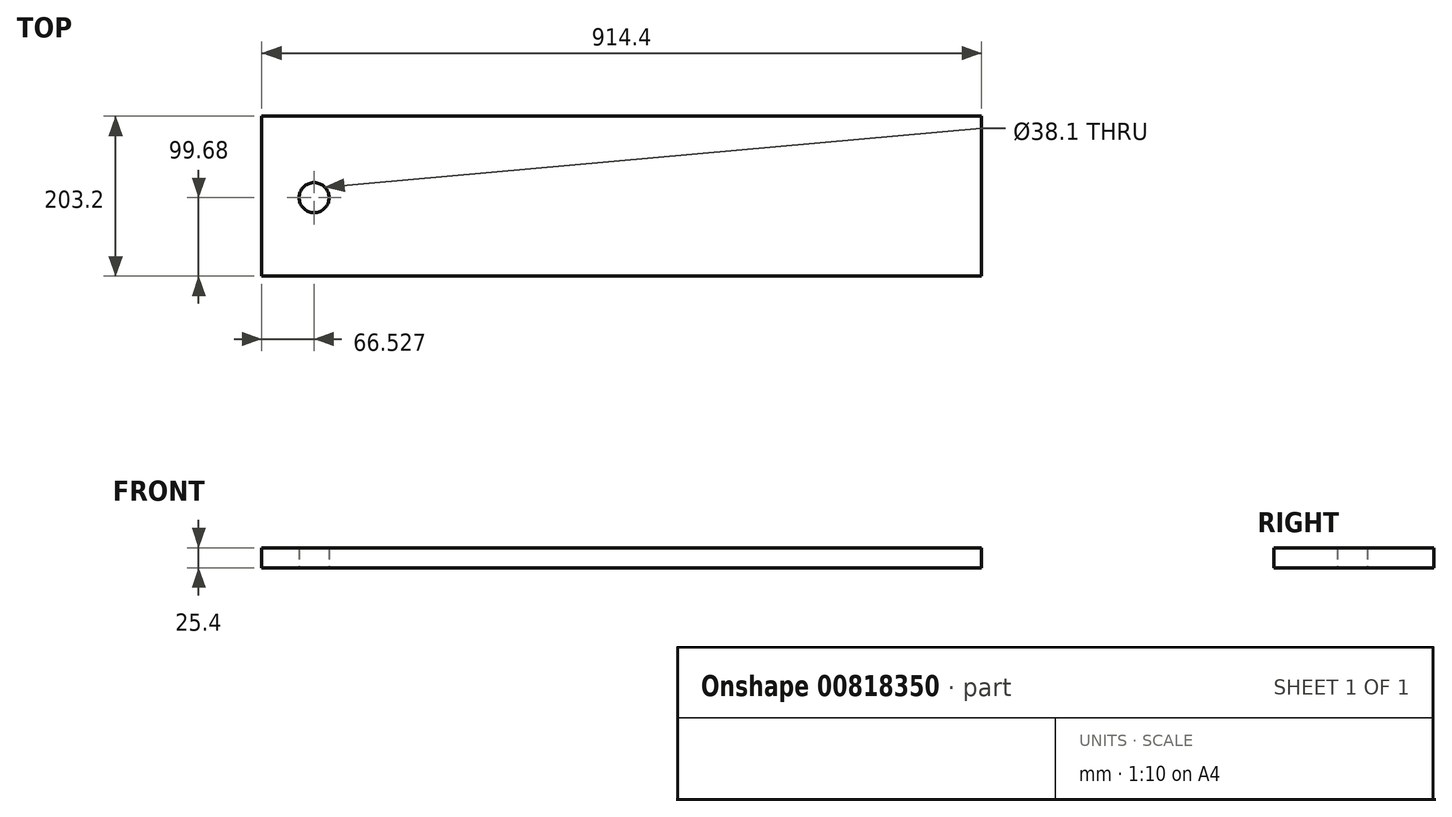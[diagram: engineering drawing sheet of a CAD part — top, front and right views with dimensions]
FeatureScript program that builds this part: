
annotation { "Feature Type Name" : "Feature", "Feature Type Description" : "" }
export const myFeature = defineFeature(function(context is Context, id is Id, definition is map)
    precondition{}
    {
        {
            var Q0;
            Q0=qCreatedBy(makeId("Top.planeOp"),FACE);
            var sketch = newSketch(context, id + "F0", { "sketchPlane" : qUnion([Q0])});
            skLineSegment(sketch, "E0.bottom", {"start": v(-470.18, 103.52) * mm, "end": v(444.22, 103.52) * mm});
            skLineSegment(sketch, "E0.top", {"start": v(-470.18, -99.68) * mm, "end": v(444.22, -99.68) * mm});
            skLineSegment(sketch, "E0.left", {"start": v(-470.18, 103.52) * mm, "end": v(-470.18, -99.68) * mm});
            skLineSegment(sketch, "E0.right", {"start": v(444.22, 103.52) * mm, "end": v(444.22, -99.68) * mm});
            skCircle(sketch, "E1", {"center": v(-403.65, 0) * mm, "radius": 19.05 * mm});
            skSolve(sketch);
        }
        {
            var Q0;
            Q0 = qSketchRegion(id + "F0", true);
            var Q1;
            Q1=makeQuery(id+"F0.imprint","IMPRINT",FACE,{"disambiguationData":[TD([[makeQuery(id+"F0.imprint","IMPRINT",EDGE,{"derivedFrom":sQuery(id+"F0.wireOp",EDGE,"E0.bottom")}),-1.0]])]});
            extrude(context, id + "F1", {"entities" : qUnion([Q0, Q1]), "depth" : 25.4 * mm, "offsetDistance" : 25.4 * mm});
        }
    });
